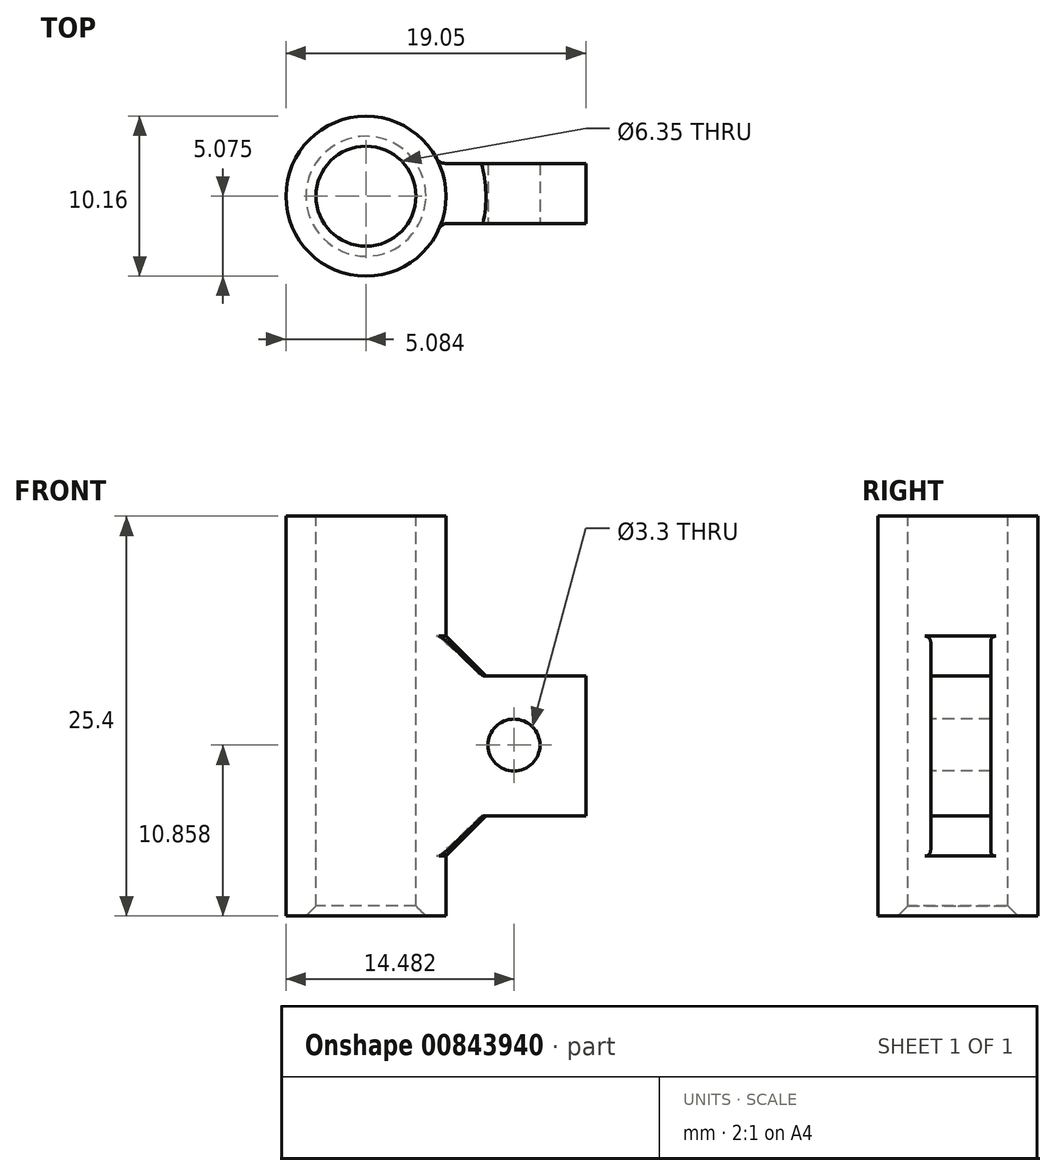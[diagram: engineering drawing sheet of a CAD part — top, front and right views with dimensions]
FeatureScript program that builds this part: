
annotation { "Feature Type Name" : "Feature", "Feature Type Description" : "" }
export const myFeature = defineFeature(function(context is Context, id is Id, definition is map)
    precondition{}
    {
        {
            var Q0;
            Q0=qCreatedBy(makeId("Top.planeOp"),FACE);
            var sketch = newSketch(context, id + "F0", { "sketchPlane" : qUnion([Q0])});
            skLineSegment(sketch, "E0.bottom", {"start": v(-30.7, -34.18) * mm, "end": v(-40.86, -34.18) * mm});
            skLineSegment(sketch, "E0.top", {"start": v(-30.7, -44.34) * mm, "end": v(-40.86, -44.34) * mm});
            skLineSegment(sketch, "E0.left", {"start": v(-30.7, -34.18) * mm, "end": v(-30.7, -44.34) * mm});
            skLineSegment(sketch, "E0.right", {"start": v(-40.86, -34.18) * mm, "end": v(-40.86, -44.34) * mm});
            skPoint(sketch, "E0.middle", {"position": v(-35.78, -39.26) * mm});
            skSolve(sketch);
        }
        {
            var Q0;
            Q0=makeQuery(id+"F0.imprint","IMPRINT",FACE,{"disambiguationData":[TD([[makeQuery(id+"F0.imprint","IMPRINT",EDGE,{"derivedFrom":sQuery(id+"F0.wireOp",EDGE,"E0.bottom")}),1.0]])]});
            extrude(context, id + "F1", {"entities" : qUnion([Q0]), "depth" : 25.4 * mm, "offsetDistance" : 25.4 * mm});
        }
        {
            var Q0;
            Q0=makeQuery(id+"F1.opExtrude","CAP_FACE",FACE,{"disambiguationData":[OSD([sQuery(id+"F0.wireOp",EDGE,"E0.bottom"),sQuery(id+"F0.wireOp",EDGE,"E0.top"),sQuery(id+"F0.wireOp",EDGE,"E0.left"),sQuery(id+"F0.wireOp",EDGE,"E0.right")])],"isStart":false});
            var sketch = newSketch(context, id + "F2", { "sketchPlane" : qUnion([Q0])});
            skCircle(sketch, "E1", {"center": v(-35.78, -39.26) * mm, "radius": 3.18 * mm});
            skSolve(sketch);
        }
        {
            var Q0;
            Q0=makeQuery(id+"F2.imprint","IMPRINT",FACE,{"disambiguationData":[TD([[makeQuery(id+"F2.imprint","IMPRINT",EDGE,{"derivedFrom":sQuery(id+"F2.wireOp",EDGE,"E1")}),1.0]])]});
            extrude(context, id + "F3", {"entities" : qUnion([Q0]), "operationType" : NewBodyOperationType.REMOVE, "oppositeDirection" : true, "depth" : 38.1 * mm, "offsetDistance" : 25.4 * mm});
        }
        {
            var Q0;
            Q0=makeQuery(id+"F3.boolean.opBoolean","INTERSECT",EDGE,{"derivedFrom":[makeQuery(id+"FBT6w4xs5Hqvy3s_1.boolean.opBoolean","MERGE",FACE,{"derivedFrom":[makeQuery(id+"F1.opExtrude","CAP_FACE",FACE,{"disambiguationData":[OSD([sQuery(id+"F0.wireOp",EDGE,"E0.bottom"),sQuery(id+"F0.wireOp",EDGE,"E0.top"),sQuery(id+"F0.wireOp",EDGE,"E0.left"),sQuery(id+"F0.wireOp",EDGE,"E0.right")])],"isStart":true}),makeQuery(id+"FBT6w4xs5Hqvy3s_1.opExtrude","SWEPT_FACE",FACE,{"disambiguationData":[OSD([sQuery(id+"FYnukvY2m7MVSni_1.wireOp",EDGE,"5XcZ7HQe-gcln-zMP8-hORr-0zm2ugMAU7pb.bottom")])]})]}),makeQuery(id+"F3.opExtrude","SWEPT_FACE",FACE,{"disambiguationData":[OSD([sQuery(id+"F2.wireOp",EDGE,"E1")])]})]});
            chamfer(context, id + "F4", {"entities" : qUnion([Q0]), "width" : 0.64 * mm, "tangentPropagation" : true});
        }
        {
            var Q0;
            Q0=makeQuery(id+"F1.opExtrude","SWEPT_FACE",FACE,{"disambiguationData":[OSD([sQuery(id+"F0.wireOp",EDGE,"E0.left")])]});
            var sketch = newSketch(context, id + "F5", { "sketchPlane" : qUnion([Q0])});
            skLineSegment(sketch, "E2.bottom", {"start": v(-40.99, 15.24) * mm, "end": v(-37.18, 15.24) * mm});
            skLineSegment(sketch, "E2.top", {"start": v(-40.99, 6.35) * mm, "end": v(-37.18, 6.35) * mm});
            skLineSegment(sketch, "E2.left", {"start": v(-40.99, 15.24) * mm, "end": v(-40.99, 6.35) * mm});
            skLineSegment(sketch, "E2.right", {"start": v(-37.18, 15.24) * mm, "end": v(-37.18, 6.35) * mm});
            skSolve(sketch);
        }
        {
            var Q0;
            Q0=makeQuery(id+"F5.imprint","IMPRINT",FACE,{"disambiguationData":[TD([[makeQuery(id+"F5.imprint","IMPRINT",EDGE,{"derivedFrom":sQuery(id+"F5.wireOp",EDGE,"E2.bottom")}),-1.0]])]});
            extrude(context, id + "F6", {"entities" : qUnion([Q0]), "operationType" : NewBodyOperationType.ADD, "depth" : 8.9 * mm, "offsetDistance" : 25.4 * mm});
        }
        {
            var Q0;
            Q0=makeQuery(id+"F1.opExtrude","SWEPT_EDGE",EDGE,{"disambiguationData":[OSD([sQuery(id+"F0.wireOp",EDGE,"E0.top"),sQuery(id+"F0.wireOp",EDGE,"E0.left")])]});
            var Q1;
            Q1=makeQuery(id+"F1.opExtrude","SWEPT_EDGE",EDGE,{"disambiguationData":[OSD([sQuery(id+"F0.wireOp",EDGE,"E0.bottom"),sQuery(id+"F0.wireOp",EDGE,"E0.left")])]});
            var Q2;
            Q2=makeQuery(id+"F1.opExtrude","SWEPT_EDGE",EDGE,{"disambiguationData":[OSD([sQuery(id+"F0.wireOp",EDGE,"E0.top"),sQuery(id+"F0.wireOp",EDGE,"E0.right")])]});
            var Q3;
            Q3=makeQuery(id+"F1.opExtrude","SWEPT_EDGE",EDGE,{"disambiguationData":[OSD([sQuery(id+"F0.wireOp",EDGE,"E0.bottom"),sQuery(id+"F0.wireOp",EDGE,"E0.right")])]});
            fillet(context, id + "F7", {"entities" : qUnion([Q0, Q1, Q2, Q3]), "radius" : 5.08 * mm, "tangentPropagation" : true, "allowEdgeOverflow" : false});
        }
        {
            var Q0;
            Q0=makeQuery(id+"F7.opFillet","BLEND_EDGE",EDGE,{"blendedFrom":[makeQuery(id+"F1.opExtrude","SWEPT_EDGE",EDGE,{"disambiguationData":[OSD([sQuery(id+"F0.wireOp",EDGE,"E0.bottom"),sQuery(id+"F0.wireOp",EDGE,"E0.left")])]}),makeQuery(id+"F6.opExtrude","SWEPT_FACE",FACE,{"disambiguationData":[OSD([sQuery(id+"F5.wireOp",EDGE,"E2.bottom")])]})],"blendedInto":[makeQuery(id+"F6.opExtrude","SWEPT_FACE",FACE,{"disambiguationData":[OSD([sQuery(id+"F5.wireOp",EDGE,"E2.bottom")])]})]});
            var Q1;
            Q1=makeQuery(id+"F7.opFillet","BLEND_EDGE",EDGE,{"blendedFrom":[makeQuery(id+"F1.opExtrude","SWEPT_EDGE",EDGE,{"disambiguationData":[OSD([sQuery(id+"F0.wireOp",EDGE,"E0.bottom"),sQuery(id+"F0.wireOp",EDGE,"E0.left")])]}),makeQuery(id+"F6.opExtrude","SWEPT_FACE",FACE,{"disambiguationData":[OSD([sQuery(id+"F5.wireOp",EDGE,"E2.top")])]})],"blendedInto":[makeQuery(id+"F6.opExtrude","SWEPT_FACE",FACE,{"disambiguationData":[OSD([sQuery(id+"F5.wireOp",EDGE,"E2.top")])]})]});
            chamfer(context, id + "F8", {"entities" : qUnion([Q0, Q1]), "width" : 2.54 * mm, "tangentPropagation" : true});
        }
        {
            var Q0;
            Q0=makeQuery(id+"F6.opExtrude","SWEPT_FACE",FACE,{"disambiguationData":[OSD([sQuery(id+"F5.wireOp",EDGE,"E2.left")])]});
            var sketch = newSketch(context, id + "F9", { "sketchPlane" : qUnion([Q0])});
            skCircle(sketch, "E3", {"center": v(-26.38, 10.86) * mm, "radius": 1.65 * mm});
            skSolve(sketch);
        }
        {
            var Q0;
            Q0=makeQuery(id+"F9.imprint","IMPRINT",FACE,{"disambiguationData":[TD([[makeQuery(id+"F9.imprint","IMPRINT",EDGE,{"derivedFrom":sQuery(id+"F9.wireOp",EDGE,"E3")}),1.0]])]});
            extrude(context, id + "F10", {"entities" : qUnion([Q0]), "operationType" : NewBodyOperationType.REMOVE, "oppositeDirection" : true, "depth" : 25.4 * mm, "offsetDistance" : 25.4 * mm});
        }
        {
            var Q0;
            Q0=makeQuery(id+"F7.opFillet","BLEND_EDGE",EDGE,{"blendedFrom":[makeQuery(id+"F1.opExtrude","SWEPT_EDGE",EDGE,{"disambiguationData":[OSD([sQuery(id+"F0.wireOp",EDGE,"E0.top"),sQuery(id+"F0.wireOp",EDGE,"E0.left")])]}),makeQuery(id+"F6.opExtrude","SWEPT_FACE",FACE,{"disambiguationData":[OSD([sQuery(id+"F5.wireOp",EDGE,"E2.left")])]})],"blendedInto":[makeQuery(id+"F6.opExtrude","SWEPT_FACE",FACE,{"disambiguationData":[OSD([sQuery(id+"F5.wireOp",EDGE,"E2.left")])]})]});
            var Q1;
            Q1=makeQuery(id+"F7.opFillet","BLEND_EDGE",EDGE,{"blendedFrom":[makeQuery(id+"F1.opExtrude","SWEPT_EDGE",EDGE,{"disambiguationData":[OSD([sQuery(id+"F0.wireOp",EDGE,"E0.bottom"),sQuery(id+"F0.wireOp",EDGE,"E0.left")])]}),makeQuery(id+"F6.opExtrude","SWEPT_FACE",FACE,{"disambiguationData":[OSD([sQuery(id+"F5.wireOp",EDGE,"E2.right")])]})],"blendedInto":[makeQuery(id+"F6.opExtrude","SWEPT_FACE",FACE,{"disambiguationData":[OSD([sQuery(id+"F5.wireOp",EDGE,"E2.right")])]})]});
            fillet(context, id + "F11", {"entities" : qUnion([Q0, Q1]), "radius" : 0.64 * mm, "tangentPropagation" : true, "allowEdgeOverflow" : false});
        }
    });
